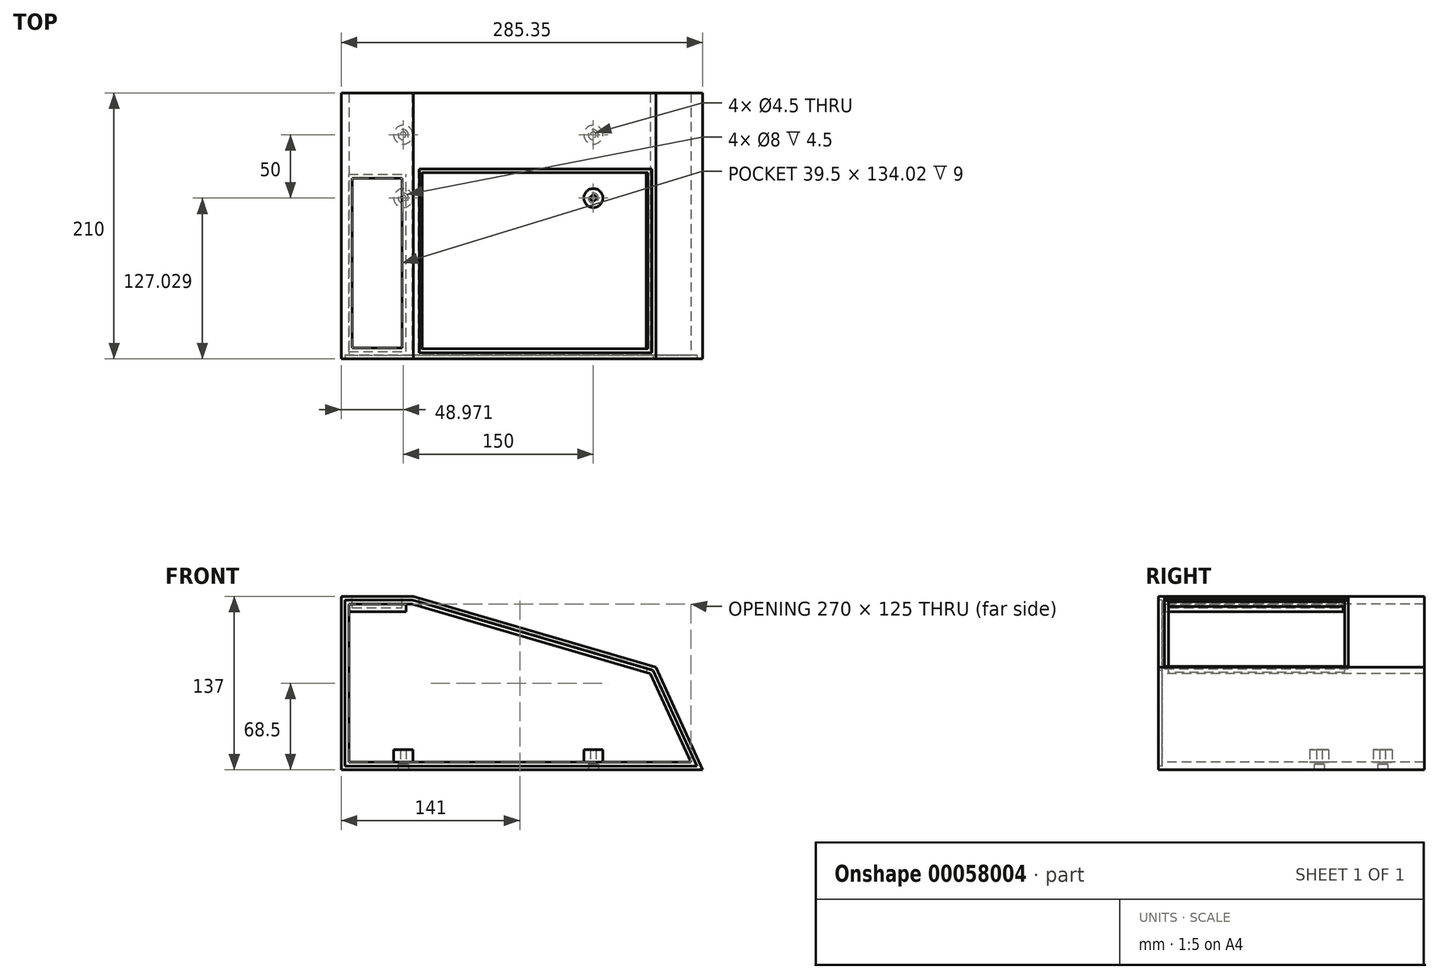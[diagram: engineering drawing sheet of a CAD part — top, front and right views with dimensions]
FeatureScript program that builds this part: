
annotation { "Feature Type Name" : "Feature", "Feature Type Description" : "" }
export const myFeature = defineFeature(function(context is Context, id is Id, definition is map)
    precondition{}
    {
        {
            assignVariable(context, id + "F0", {"name" : "width", "anyValue" : 210});
        }
        {
            var Q0;
            Q0=qCreatedBy(makeId("Front.planeOp"),FACE);
            var sketch = newSketch(context, id + "F1", { "sketchPlane" : qUnion([Q0])});
            skLineSegment(sketch, "E0", {"start": v(0, 0) * mm, "end": v(270, 0) * mm});
            skLineSegment(sketch, "E1", {"start": v(270, 0) * mm, "end": v(237.92, 70) * mm});
            skLineSegment(sketch, "E2", {"start": v(237.92, 70) * mm, "end": v(50, 125) * mm});
            skLineSegment(sketch, "E3", {"start": v(50, 125) * mm, "end": v(0, 125) * mm});
            skLineSegment(sketch, "E4", {"start": v(0, 125) * mm, "end": v(0, 0) * mm});
            skLineSegment(sketch, "E5", {"start": v(237.92, 70) * mm, "end": v(237.92, 0) * mm, "construction": true});
            skLineSegment(sketch, "E6.0", {"start": v(-6, 131) * mm, "end": v(-6, -6) * mm});
            skLineSegment(sketch, "E6.1", {"start": v(50.86, 131) * mm, "end": v(-6, 131) * mm});
            skLineSegment(sketch, "E6.2", {"start": v(-6, -6) * mm, "end": v(279.35, -6) * mm});
            skLineSegment(sketch, "E6.3", {"start": v(279.35, -6) * mm, "end": v(242.24, 74.99) * mm});
            skLineSegment(sketch, "E6.4", {"start": v(242.24, 74.99) * mm, "end": v(50.86, 131) * mm});
            skLineSegment(sketch, "E7.0", {"start": v(274.67, -3) * mm, "end": v(240.08, 72.5) * mm});
            skLineSegment(sketch, "E7.1", {"start": v(-3, -3) * mm, "end": v(274.67, -3) * mm});
            skLineSegment(sketch, "E7.2", {"start": v(240.08, 72.5) * mm, "end": v(50.43, 128) * mm});
            skLineSegment(sketch, "E7.3", {"start": v(50.43, 128) * mm, "end": v(-3, 128) * mm});
            skLineSegment(sketch, "E7.4", {"start": v(-3, 128) * mm, "end": v(-3, -3) * mm});
            skSolve(sketch);
        }
        {
            var Q0;
            Q0=makeQuery(id+"F1.imprint","IMPRINT",FACE,{"disambiguationData":[TD([[makeQuery(id+"F1.imprint","IMPRINT",EDGE,{"derivedFrom":sQuery(id+"F1.wireOp",EDGE,"E0")}),-1.0]])]});
            var Q1;
            Q1=makeQuery(id+"F1.imprint","IMPRINT",FACE,{"disambiguationData":[TD([[makeQuery(id+"F1.imprint","IMPRINT",EDGE,{"derivedFrom":sQuery(id+"F1.wireOp",EDGE,"E6.0")}),1.0]])]});
            extrude(context, id + "F2", {"entities" : qUnion([Q0, Q1]), "oppositeDirection" : true, "depth" : (getVariable(context, 'width')) * mm});
        }
        {
            var Q0;
            Q0=makeQuery(id+"F2.opExtrude","SWEPT_FACE",FACE,{"disambiguationData":[OSD([sQuery(id+"F1.wireOp",EDGE,"E6.2")])]});
            var sketch = newSketch(context, id + "F3", { "sketchPlane" : qUnion([Q0])});
            skCircle(sketch, "E8", {"center": v(42.97, -177.03) * mm, "radius": 7.5 * mm});
            skCircle(sketch, "E9", {"center": v(42.97, -127.03) * mm, "radius": 7.5 * mm});
            skCircle(sketch, "E10", {"center": v(192.97, -127.03) * mm, "radius": 7.5 * mm});
            skCircle(sketch, "E11", {"center": v(192.97, -177.03) * mm, "radius": 7.5 * mm});
            skLineSegment(sketch, "E12.bottom", {"start": v(42.97, -177.03) * mm, "end": v(192.97, -177.03) * mm, "construction": true});
            skLineSegment(sketch, "E12.top", {"start": v(42.97, -127.03) * mm, "end": v(192.97, -127.03) * mm, "construction": true});
            skLineSegment(sketch, "E12.left", {"start": v(42.97, -177.03) * mm, "end": v(42.97, -127.03) * mm, "construction": true});
            skLineSegment(sketch, "E12.right", {"start": v(192.97, -177.03) * mm, "end": v(192.97, -127.03) * mm, "construction": true});
            skLineSegment(sketch, "E13.bottom", {"start": v(18, -202) * mm, "end": v(217.94, -202) * mm, "construction": true});
            skLineSegment(sketch, "E13.top", {"start": v(18, -102.06) * mm, "end": v(217.94, -102.06) * mm, "construction": true});
            skLineSegment(sketch, "E13.left", {"start": v(18, -202) * mm, "end": v(18, -102.06) * mm, "construction": true});
            skLineSegment(sketch, "E13.right", {"start": v(217.94, -202) * mm, "end": v(217.94, -102.06) * mm, "construction": true});
            skLineSegment(sketch, "E14", {"start": v(42.97, -177.03) * mm, "end": v(18, -177.03) * mm, "construction": true});
            skLineSegment(sketch, "E15", {"start": v(42.97, -177.03) * mm, "end": v(42.97, -202) * mm, "construction": true});
            skLineSegment(sketch, "E16", {"start": v(192.97, -127.03) * mm, "end": v(192.97, -102.06) * mm, "construction": true});
            skLineSegment(sketch, "E17", {"start": v(192.97, -127.03) * mm, "end": v(217.94, -127.03) * mm, "construction": true});
            skSolve(sketch);
        }
        {
            var Q0;
            Q0=makeQuery(id+"F2.opExtrude","SWEPT_FACE",FACE,{"disambiguationData":[OSD([sQuery(id+"F1.wireOp",EDGE,"E6.4")])]});
            var sketch = newSketch(context, id + "F4", { "sketchPlane" : qUnion([Q0])});
            skLineSegment(sketch, "E18.bottom", {"start": v(17.02, 5) * mm, "end": v(208.42, 5) * mm});
            skLineSegment(sketch, "E18.top", {"start": v(17.02, 150) * mm, "end": v(208.42, 150) * mm});
            skLineSegment(sketch, "E18.left", {"start": v(17.02, 5) * mm, "end": v(17.02, 150) * mm});
            skLineSegment(sketch, "E18.right", {"start": v(208.42, 5) * mm, "end": v(208.42, 150) * mm});
            skLineSegment(sketch, "E19.bottom", {"start": v(20.02, 8) * mm, "end": v(205.42, 8) * mm});
            skLineSegment(sketch, "E19.top", {"start": v(20.02, 147) * mm, "end": v(205.42, 147) * mm});
            skLineSegment(sketch, "E19.left", {"start": v(20.02, 8) * mm, "end": v(20.02, 147) * mm});
            skLineSegment(sketch, "E19.right", {"start": v(205.42, 8) * mm, "end": v(205.42, 147) * mm});
            skLineSegment(sketch, "E20", {"start": v(17.02, 5) * mm, "end": v(17.02, 0) * mm, "construction": true});
            skLineSegment(sketch, "E21", {"start": v(17.02, 5) * mm, "end": v(12.02, 5) * mm, "construction": true});
            skLineSegment(sketch, "E22", {"start": v(20.02, 8) * mm, "end": v(20.02, 5) * mm, "construction": true});
            skLineSegment(sketch, "E23", {"start": v(20.02, 8) * mm, "end": v(17.02, 8) * mm, "construction": true});
            skLineSegment(sketch, "E24", {"start": v(205.42, 147) * mm, "end": v(208.42, 147) * mm, "construction": true});
            skLineSegment(sketch, "E25", {"start": v(208.42, 150) * mm, "end": v(211.42, 150) * mm, "construction": true});
            skLineSegment(sketch, "E26", {"start": v(208.42, 150) * mm, "end": v(208.42, 210) * mm, "construction": true});
            skLineSegment(sketch, "E27", {"start": v(205.42, 147) * mm, "end": v(205.42, 150) * mm, "construction": true});
            skSolve(sketch);
        }
        {
            var Q0;
            Q0=makeQuery(id+"F4.imprint","IMPRINT",FACE,{"disambiguationData":[TD([[makeQuery(id+"F4.imprint","IMPRINT",EDGE,{"derivedFrom":sQuery(id+"F4.wireOp",EDGE,"E19.bottom")}),1.0]])]});
            var Q1;
            Q1=makeQuery(id+"F2.opExtrude","SWEPT_FACE",FACE,{"disambiguationData":[OSD([sQuery(id+"F1.wireOp",EDGE,"E2")])]});
            var Q2;
            Q2=makeQuery(id+"F2.opExtrude","SWEPT_BODY",BODY,{"disambiguationData":[OSD([sQuery(id+"F1.wireOp",EDGE,"E0"),sQuery(id+"F1.wireOp",EDGE,"E1"),sQuery(id+"F1.wireOp",EDGE,"E2"),sQuery(id+"F1.wireOp",EDGE,"E3"),sQuery(id+"F1.wireOp",EDGE,"E4"),sQuery(id+"F1.wireOp",EDGE,"E6.0"),sQuery(id+"F1.wireOp",EDGE,"E6.1"),sQuery(id+"F1.wireOp",EDGE,"E6.2"),sQuery(id+"F1.wireOp",EDGE,"E6.3"),sQuery(id+"F1.wireOp",EDGE,"E6.4")])]});
            extrude(context, id + "F5", {"entities" : qUnion([Q0]), "operationType" : NewBodyOperationType.REMOVE, "endBound" : BoundingType.UP_TO_BODY, "oppositeDirection" : true, "endBoundEntityFace" : qUnion([Q1]), "endBoundEntityBody" : qUnion([Q2]), "depth" : 25 * mm});
        }
        {
            var Q0;
            Q0=makeQuery(id+"F4.imprint","IMPRINT",FACE,{"disambiguationData":[TD([[makeQuery(id+"F4.imprint","IMPRINT",EDGE,{"derivedFrom":sQuery(id+"F4.wireOp",EDGE,"E18.bottom")}),1.0]])]});
            extrude(context, id + "F6", {"entities" : qUnion([Q0]), "operationType" : NewBodyOperationType.REMOVE, "oppositeDirection" : true, "depth" : 2 * mm});
        }
        {
            var Q0;
            Q0=makeQuery(id+"F2.opExtrude","SWEPT_FACE",FACE,{"disambiguationData":[OSD([sQuery(id+"F1.wireOp",EDGE,"E6.1")])]});
            var sketch = newSketch(context, id + "F7", { "sketchPlane" : qUnion([Q0])});
            skLineSegment(sketch, "E28.bottom", {"start": v(2.68, 8.68) * mm, "end": v(42.18, 8.68) * mm});
            skLineSegment(sketch, "E28.top", {"start": v(2.68, 142.7) * mm, "end": v(42.18, 142.7) * mm});
            skLineSegment(sketch, "E28.left", {"start": v(2.68, 8.68) * mm, "end": v(2.68, 142.7) * mm});
            skLineSegment(sketch, "E28.right", {"start": v(42.18, 8.68) * mm, "end": v(42.18, 142.7) * mm});
            skLineSegment(sketch, "E29", {"start": v(2.68, 8.68) * mm, "end": v(-6, 8.68) * mm, "construction": true});
            skLineSegment(sketch, "E30", {"start": v(2.68, 8.68) * mm, "end": v(2.68, 0) * mm, "construction": true});
            skLineSegment(sketch, "E31", {"start": v(42.18, 8.68) * mm, "end": v(50.86, 8.68) * mm, "construction": true});
            skLineSegment(sketch, "E32.0", {"start": v(-0.32, 145.7) * mm, "end": v(45.18, 145.7) * mm});
            skLineSegment(sketch, "E32.1", {"start": v(-0.32, 5.68) * mm, "end": v(-0.32, 145.7) * mm});
            skLineSegment(sketch, "E32.2", {"start": v(-0.32, 5.68) * mm, "end": v(45.18, 5.68) * mm});
            skLineSegment(sketch, "E32.3", {"start": v(45.18, 5.68) * mm, "end": v(45.18, 145.7) * mm});
            skSolve(sketch);
        }
        {
            var Q0;
            Q0=makeQuery(id+"F7.imprint","IMPRINT",FACE,{"disambiguationData":[TD([[makeQuery(id+"F7.imprint","IMPRINT",EDGE,{"derivedFrom":sQuery(id+"F7.wireOp",EDGE,"E28.bottom")}),1.0]])]});
            var Q1;
            Q1=makeQuery(id+"F7.imprint","IMPRINT",FACE,{"disambiguationData":[TD([[makeQuery(id+"F7.imprint","IMPRINT",EDGE,{"derivedFrom":sQuery(id+"F7.wireOp",EDGE,"E28.bottom")}),-1.0]])]});
            extrude(context, id + "F8", {"entities" : qUnion([Q0, Q1]), "operationType" : NewBodyOperationType.ADD, "oppositeDirection" : true, "depth" : 12 * mm});
        }
        {
            var Q0;
            Q0=makeQuery(id+"F7.imprint","IMPRINT",FACE,{"disambiguationData":[TD([[makeQuery(id+"F7.imprint","IMPRINT",EDGE,{"derivedFrom":sQuery(id+"F7.wireOp",EDGE,"E28.bottom")}),1.0]])]});
            extrude(context, id + "F9", {"entities" : qUnion([Q0]), "operationType" : NewBodyOperationType.REMOVE, "oppositeDirection" : true, "depth" : 9 * mm});
        }
        {
            var Q0;
            Q0=makeQuery(id+"F1.imprint","IMPRINT",FACE,{"disambiguationData":[TD([[makeQuery(id+"F1.imprint","IMPRINT",EDGE,{"derivedFrom":sQuery(id+"F1.wireOp",EDGE,"E0")}),-1.0]])]});
            extrude(context, id + "F10", {"entities" : qUnion([Q0]), "operationType" : NewBodyOperationType.REMOVE, "oppositeDirection" : true, "depth" : 3 * mm});
        }
        {
            var Q0;
            Q0=makeQuery(id+"F3.imprint","IMPRINT",FACE,{"disambiguationData":[TD([[makeQuery(id+"F3.imprint","IMPRINT",EDGE,{"derivedFrom":sQuery(id+"F3.wireOp",EDGE,"E11")}),1.0]])]});
            var Q1;
            Q1=makeQuery(id+"F3.imprint","IMPRINT",FACE,{"disambiguationData":[TD([[makeQuery(id+"F3.imprint","IMPRINT",EDGE,{"derivedFrom":sQuery(id+"F3.wireOp",EDGE,"E10")}),1.0]])]});
            var Q2;
            Q2=makeQuery(id+"F3.imprint","IMPRINT",FACE,{"disambiguationData":[TD([[makeQuery(id+"F3.imprint","IMPRINT",EDGE,{"derivedFrom":sQuery(id+"F3.wireOp",EDGE,"E8")}),1.0]])]});
            var Q3;
            Q3=makeQuery(id+"F3.imprint","IMPRINT",FACE,{"disambiguationData":[TD([[makeQuery(id+"F3.imprint","IMPRINT",EDGE,{"derivedFrom":sQuery(id+"F3.wireOp",EDGE,"E9")}),1.0]])]});
            extrude(context, id + "F11", {"entities" : qUnion([Q0, Q1, Q2, Q3]), "operationType" : NewBodyOperationType.ADD, "oppositeDirection" : true, "depth" : 16 * mm});
        }
        {
            var Q0;
            Q0=sQuery(id+"F3.wireOp",VERTEX,"E12.top.end");
            var Q1;
            Q1=sQuery(id+"F3.wireOp",VERTEX,"E12.right.start");
            var Q2;
            Q2=sQuery(id+"F3.wireOp",VERTEX,"E12.left.start");
            var Q3;
            Q3=sQuery(id+"F3.wireOp",VERTEX,"E12.left.end");
            var Q4;
            Q4=makeQuery(id+"F2.opExtrude","SWEPT_BODY",BODY,{"disambiguationData":[OSD([sQuery(id+"F1.wireOp",EDGE,"E0"),sQuery(id+"F1.wireOp",EDGE,"E1"),sQuery(id+"F1.wireOp",EDGE,"E2"),sQuery(id+"F1.wireOp",EDGE,"E3"),sQuery(id+"F1.wireOp",EDGE,"E4"),sQuery(id+"F1.wireOp",EDGE,"E6.0"),sQuery(id+"F1.wireOp",EDGE,"E6.1"),sQuery(id+"F1.wireOp",EDGE,"E6.2"),sQuery(id+"F1.wireOp",EDGE,"E6.3"),sQuery(id+"F1.wireOp",EDGE,"E6.4")])]});
            hole(context, id + "F12", {"style" : HoleStyle.C_BORE, "endStyle" : HoleEndStyle.BLIND, "holeDiameter" : 4.5 * mm, "cBoreDiameter" : 8 * mm, "cBoreDepth" : 4.5 * mm, "holeDepth" : 40 * mm, "locations" : qUnion([Q0, Q1, Q2, Q3]), "scope" : qUnion([Q4])});
        }
    });
